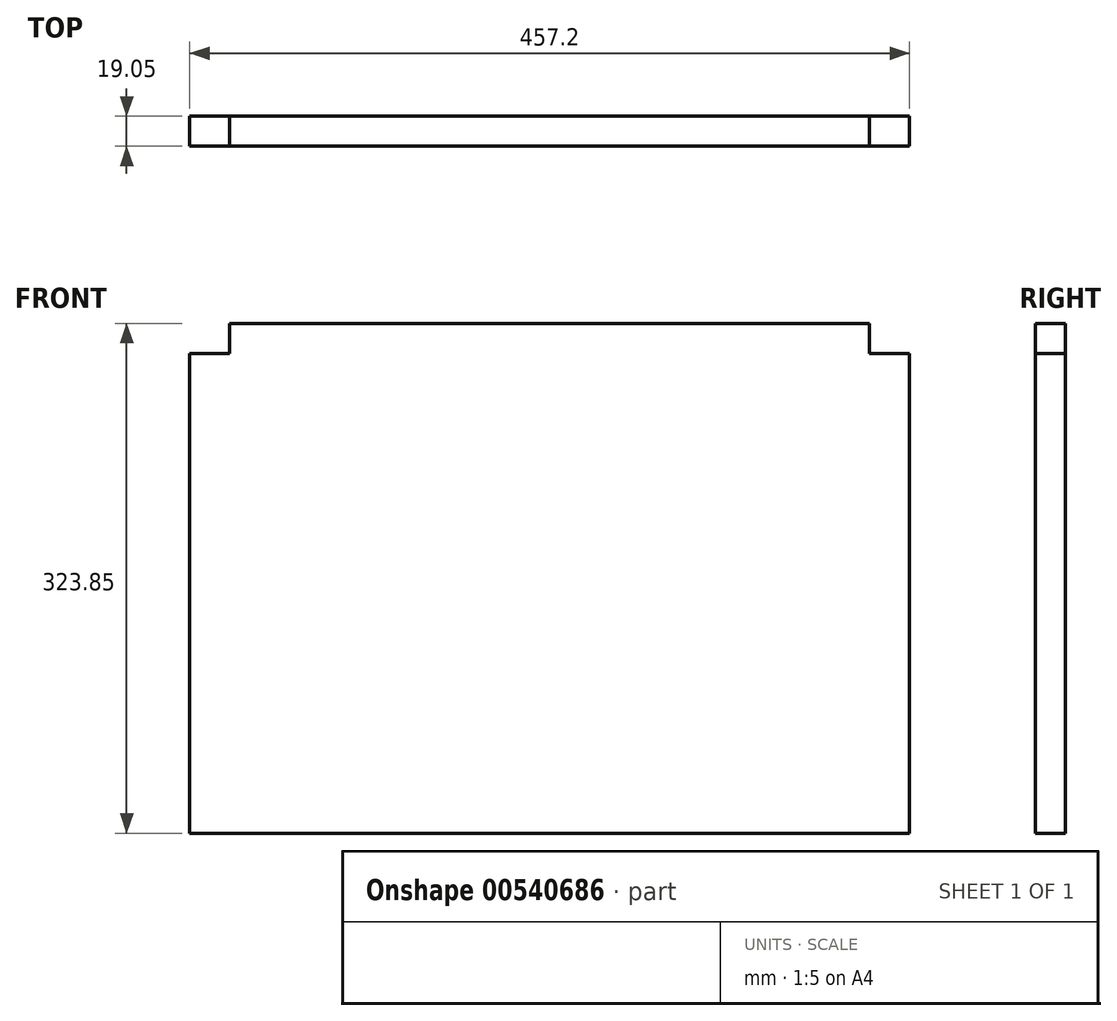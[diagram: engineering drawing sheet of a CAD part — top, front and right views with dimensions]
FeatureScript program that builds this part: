
annotation { "Feature Type Name" : "Feature", "Feature Type Description" : "" }
export const myFeature = defineFeature(function(context is Context, id is Id, definition is map)
    precondition{}
    {
        {
            var Q0;
            Q0=qCreatedBy(makeId("Front.planeOp"),FACE);
            var sketch = newSketch(context, id + "F0", { "sketchPlane" : qUnion([Q0])});
            skLineSegment(sketch, "E0.bottom", {"start": v(-229.5, 130.57) * mm, "end": v(-204.1, 130.57) * mm});
            skLineSegment(sketch, "E0.top", {"start": v(-229.5, -174.23) * mm, "end": v(227.7, -174.23) * mm});
            skLineSegment(sketch, "E0.left", {"start": v(-229.5, 130.57) * mm, "end": v(-229.5, -174.23) * mm});
            skLineSegment(sketch, "E0.right", {"start": v(227.7, 130.57) * mm, "end": v(227.7, -174.23) * mm});
            skLineSegment(sketch, "E1", {"start": v(-204.1, 130.57) * mm, "end": v(-204.1, 149.62) * mm});
            skLineSegment(sketch, "E2", {"start": v(-204.1, 149.62) * mm, "end": v(202.3, 149.62) * mm});
            skLineSegment(sketch, "E3", {"start": v(202.3, 149.62) * mm, "end": v(202.3, 130.57) * mm});
            skLineSegment(sketch, "E4.trimOffspring", {"start": v(202.3, 130.57) * mm, "end": v(227.7, 130.57) * mm});
            skSolve(sketch);
        }
        {
            var Q0;
            Q0 = qSketchRegion(id + "F0", true);
            extrude(context, id + "F1", {"entities" : qUnion([Q0]), "depth" : 19.05 * mm, "offsetDistance" : 25.4 * mm});
        }
    });
